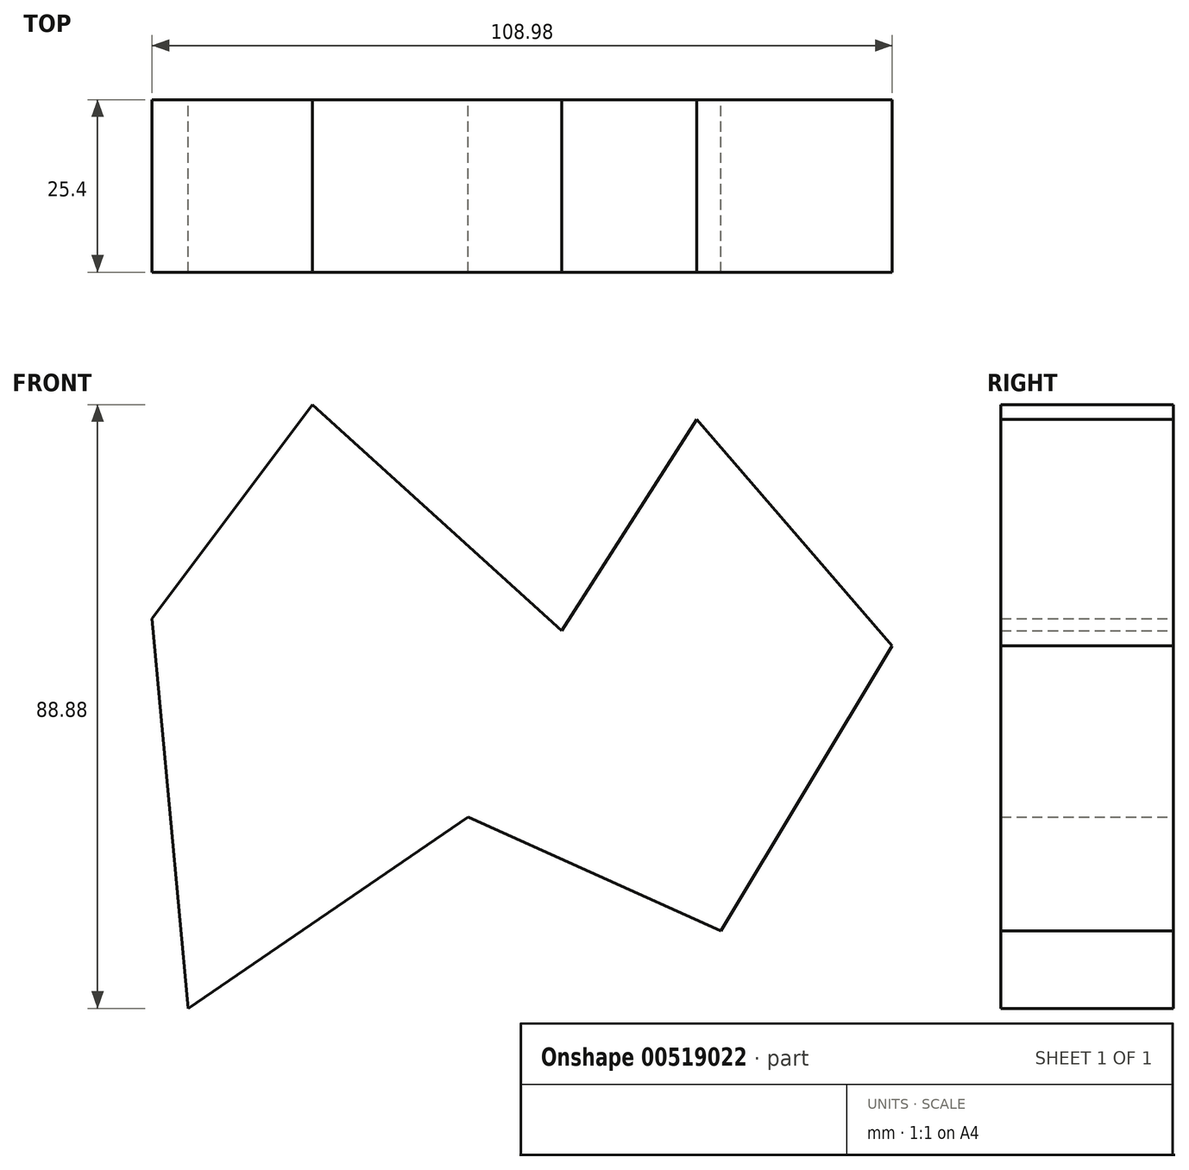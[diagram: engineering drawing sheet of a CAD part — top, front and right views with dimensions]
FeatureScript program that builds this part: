
annotation { "Feature Type Name" : "Feature", "Feature Type Description" : "" }
export const myFeature = defineFeature(function(context is Context, id is Id, definition is map)
    precondition{}
    {
        {
            var Q0;
            Q0=qCreatedBy(makeId("Front.planeOp"),FACE);
            var sketch = newSketch(context, id + "F0", { "sketchPlane" : qUnion([Q0])});
            skLineSegment(sketch, "E0", {"start": v(-32.12, 23.45) * mm, "end": v(-8.47, 54.98) * mm});
            skLineSegment(sketch, "E1", {"start": v(-8.47, 54.98) * mm, "end": v(28.18, 21.68) * mm});
            skLineSegment(sketch, "E2", {"start": v(28.18, 21.68) * mm, "end": v(48.08, 52.81) * mm});
            skLineSegment(sketch, "E3", {"start": v(48.08, 52.81) * mm, "end": v(76.86, 19.5) * mm});
            skLineSegment(sketch, "E4", {"start": v(76.86, 19.5) * mm, "end": v(51.63, -22.47) * mm});
            skLineSegment(sketch, "E5", {"start": v(51.63, -22.47) * mm, "end": v(14.39, -5.72) * mm});
            skLineSegment(sketch, "E6", {"start": v(14.39, -5.72) * mm, "end": v(-26.8, -33.9) * mm});
            skLineSegment(sketch, "E7", {"start": v(-26.8, -33.9) * mm, "end": v(-32.12, 23.45) * mm});
            skSolve(sketch);
        }
        {
            var Q0;
            Q0 = qSketchRegion(id + "F0", true);
            extrude(context, id + "F1", {"entities" : qUnion([Q0]), "depth" : 25.4 * mm, "offsetDistance" : 25.4 * mm});
        }
    });
